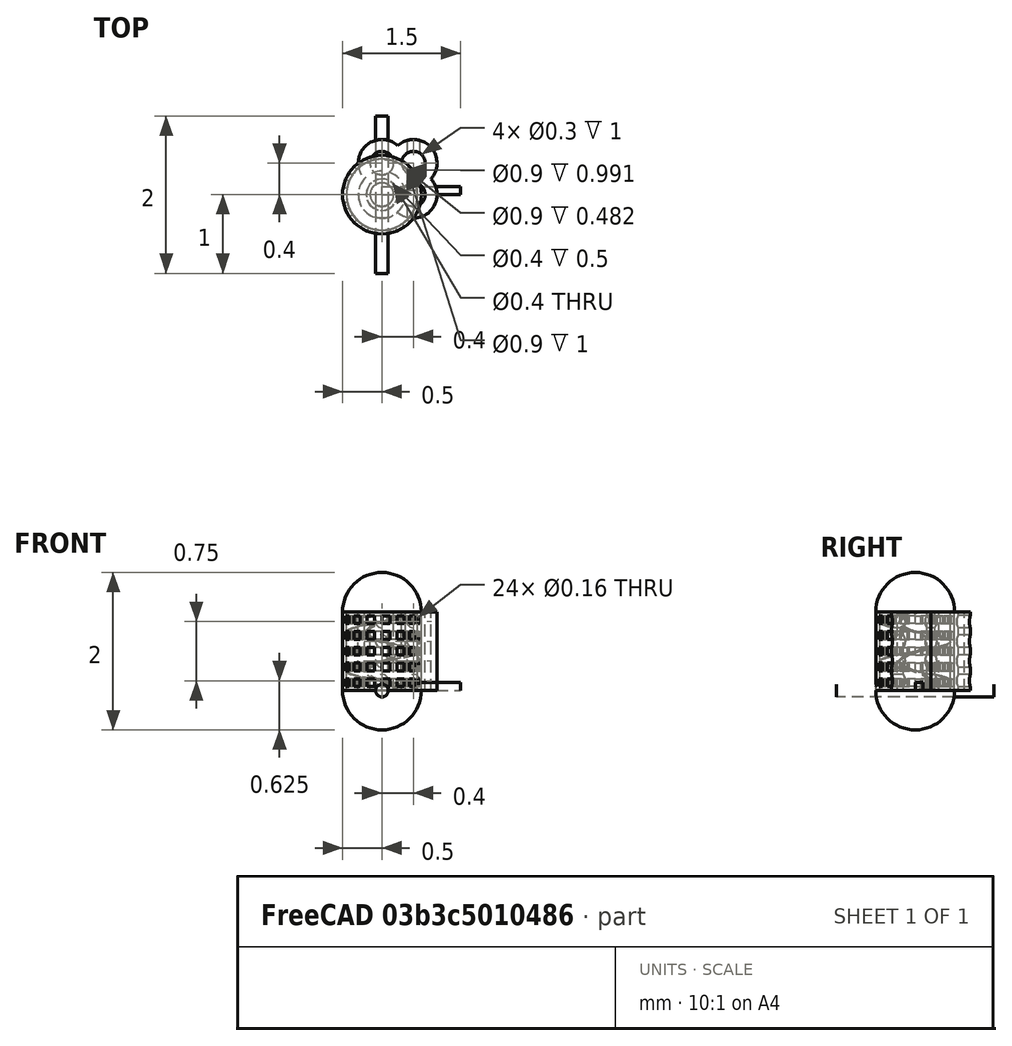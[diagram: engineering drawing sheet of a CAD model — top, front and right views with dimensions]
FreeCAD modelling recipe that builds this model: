
FCSTD DOCUMENT  (FreeCAD 0.19R24267 +99 (Git))
Label: models
License: All rights reserved
LicenseURL: http://en.wikipedia.org/wiki/All_rights_reserved
objects: Part::FeaturePython×12, Part::Cut×6, Part::Cylinder×6, Part::Box×2, Part::Sphere×2, Part::MultiFuse×2, Sketcher::SketchObject×2, PartDesign::AdditiveHelix×2, PartDesign::Body×2
note: 31 computed .brp shape members not serialized (recipe doc carries the construction recipe); baked Part::Feature solids carry a one-line shape summary decoded from their .brp

FEATURE [Part::FeaturePython] Tube  # WARN: FeaturePython — macro-defined, semantics opaque (R4)
  AttacherType = Attacher::AttachEngine3D
  Height = 1
  InnerRadius = 0.45
  OuterRadius = 0.5
FEATURE [Part::Box] Box  label="Cube"
  AttacherType = Attacher::AttachEngine3D
  Height = 0.1
  Length = 1
  Width = 0.1
FEATURE [Part::FeaturePython] Array  # Draft array (typed FeaturePython)
  Angle = 360
  ArrayType = 1
  Axis = (0,0,1)
  Base = -> Box
  Center = (0,0,0)
  Count = 16
  ExpandArray = false
  Fuse = false
  IntervalAxis = (0,0,0)
  IntervalX = (50,0,0)
  IntervalY = (0,50,0)
  IntervalZ = (0,0,50)
  NumberCircles = 3
  NumberPolar = 16
  NumberX = 2
  NumberY = 2
  NumberZ = 1
  PlacementList = 16 placements: [(0,0,0),(0,0,0),(0,0,0),(0,0,0),(0,0,0),(0,0,0),(0,0,0),(0,0,0),(0,0,0),(0,0,0),(0,0,0),(0,0,0),(0,0,0),(0,0,0),(0,0,0),(0,0,0)]
  RadialDistance = 50
  ScaleList = (16) [(1,1,1),(1,1,1),(1,1,1),(1,1,1),(1,1,1),(1,1,1),(1,1,1),(1,1,1),(1,1,1),(1,1,1),(1,1,1),(1,1,1),(1,1,1),(1,1,1),(1,1,1),(1,1,1)]
  Symmetry = 1
  TangentialDistance = 25
FEATURE [Part::FeaturePython] Array001  # Draft array (typed FeaturePython)
  Angle = 360
  ArrayType = 0
  Axis = (0,0,1)
  Base = -> Array
  Center = (0,0,0)
  Count = 5
  ExpandArray = false
  Fuse = false
  IntervalAxis = (0,0,0)
  IntervalX = (100,0,0)
  IntervalY = (0,100,0)
  IntervalZ = (0,0,0.2)
  NumberCircles = 3
  NumberPolar = 5
  NumberX = 1
  NumberY = 1
  NumberZ = 5
  Placement = pos=(0,0,0.05) rot=(0,0,1;0rad)
  PlacementList = 5 placements: arithmetic series from (0,0,0) step (0,0,0.2) to (0,0,0.8)
  RadialDistance = 50
  ScaleList = (5) [(1,1,1),(1,1,1),(1,1,1),(1,1,1),(1,1,1)]
  Symmetry = 1
  TangentialDistance = 25
FEATURE [Part::Cut] Cut
  Base = -> Tube
  Tool = -> Array001
FEATURE [Part::Cylinder] Cylinder
  Angle = 360
  AttacherType = Attacher::AttachEngine3D
  Height = 1
  Radius = 0.3
FEATURE [Part::FeaturePython] Array002  # Draft array (typed FeaturePython)
  Angle = 360
  ArrayType = 0
  Axis = (0,0,1)
  Base = -> Cylinder
  Center = (0,0,0)
  Count = 4
  ExpandArray = false
  Fuse = false
  IntervalAxis = (0,0,0)
  IntervalX = (0.4,0,0)
  IntervalY = (0,0.4,0)
  IntervalZ = (0,0,100)
  NumberCircles = 3
  NumberPolar = 5
  NumberX = 2
  NumberY = 2
  NumberZ = 1
  PlacementList = 4 placements: [(0,0,0),(0,0.4,0),(0.4,0,0),(0.4,0.4,0)]
  RadialDistance = 50
  ScaleList = (4) [(1,1,1),(1,1,1),(1,1,1),(1,1,1)]
  Symmetry = 1
  TangentialDistance = 25
FEATURE [Part::FeaturePython] Connect  # WARN: FeaturePython — macro-defined, semantics opaque (R4)
  Objects = -> [Array002]
  Tolerance = 0
FEATURE [Part::Cylinder] Cylinder001
  Angle = 360
  AttacherType = Attacher::AttachEngine3D
  Height = 1
  Radius = 0.15
FEATURE [Part::FeaturePython] Array003  # Draft array (typed FeaturePython)
  Angle = 360
  ArrayType = 0
  Axis = (0,0,1)
  Base = -> Cylinder001
  Center = (0,0,0)
  Count = 4
  ExpandArray = false
  Fuse = false
  IntervalAxis = (0,0,0)
  IntervalX = (0.4,0,0)
  IntervalY = (0,0.4,0)
  IntervalZ = (0,0,100)
  NumberCircles = 3
  NumberPolar = 5
  NumberX = 2
  NumberY = 2
  NumberZ = 1
  PlacementList = 4 placements: [(0,0,0),(0,0.4,0),(0.4,0,0),(0.4,0.4,0)]
  RadialDistance = 50
  ScaleList = (4) [(1,1,1),(1,1,1),(1,1,1),(1,1,1)]
  Symmetry = 1
  TangentialDistance = 25
FEATURE [Part::Cut] Cut001
  Base = -> Connect
  Tool = -> Array003
FEATURE [Part::Cylinder] Cylinder002
  Angle = 360
  AttacherType = Attacher::AttachEngine3D
  Height = 2
  Placement = pos=(0,1,0) rot=(1,0,0;1.5708rad)
  Radius = 0.08
FEATURE [Part::FeaturePython] Array004  # Draft array (typed FeaturePython)
  Angle = 360
  ArrayType = 0
  Axis = (0,0,1)
  Base = -> Cylinder002
  Center = (0,0,0)
  Count = 8
  ExpandArray = false
  Fuse = false
  IntervalAxis = (0,0,0)
  IntervalX = (0.4,0,0)
  IntervalY = (0,100,0)
  IntervalZ = (0,0,0.25)
  NumberCircles = 3
  NumberPolar = 5
  NumberX = 2
  NumberY = 1
  NumberZ = 4
  Placement = pos=(0,0,0.125) rot=(0,0,1;0rad)
  PlacementList = 8 placements: [(0,1,0),(0,1,0.25),(0,1,0.5),(0,1,0.75),(0.4,1,0),(0.4,1,0.25),(0.4,1,0.5),(0.4,1,0.75)]
  RadialDistance = 50
  ScaleList = (8) [(1,1,1),(1,1,1),(1,1,1),(1,1,1),(1,1,1),(1,1,1),(1,1,1),(1,1,1)]
  Symmetry = 1
  TangentialDistance = 25
FEATURE [Part::Cut] Cut002
  Base = -> Cut001
  Tool = -> Array004
FEATURE [Part::Sphere] Sphere
  Angle1 = -90
  Angle2 = 90
  Angle3 = 360
  AttacherType = Attacher::AttachEngine3D
  Radius = 0.5
FEATURE [Part::Cylinder] Cylinder003
  Angle = 360
  AttacherType = Attacher::AttachEngine3D
  Height = 1
  Radius = 0.5
FEATURE [Part::Sphere] Sphere001
  Angle1 = -90
  Angle2 = 90
  Angle3 = 360
  AttacherType = Attacher::AttachEngine3D
  Placement = pos=(0,0,1) rot=(0,0,1;0rad)
  Radius = 0.5
FEATURE [Part::MultiFuse] Fusion
  Shapes = -> [Sphere,Cylinder003]
FEATURE [Part::MultiFuse] Fusion001  label="capsule"
  Shapes = -> [Sphere001,Fusion]
FEATURE [Sketcher::SketchObject] Sketch
  FullyConstrained = true
  MapMode = 5
  Support = -> [XY_Plane]
  sketch-geometry (4):
    g0: LineSegment StartX=0 StartY=0 StartZ=0 EndX=0.45 EndY=0 EndZ=0
    g1: LineSegment StartX=0.45 StartY=0 StartZ=0 EndX=0.45 EndY=0.05 EndZ=0
    g2: LineSegment StartX=0.45 StartY=0.05 StartZ=0 EndX=0 EndY=0.05 EndZ=0
    g3: LineSegment StartX=0 StartY=0.05 StartZ=0 EndX=0 EndY=0 EndZ=0
  constraints (11):
    c: Coincident(g0,g1)
    c: Coincident(g1,g2)
    c: Coincident(g2,g3)
    c: Coincident(g3,g0)
    c: Horizontal(g0)
    c: Horizontal(g2)
    c: Vertical(g1)
    c: Vertical(g3)
    c: Coincident(g0,g-1)
    c: Distance(g2) = 0.45
    c: DistanceY(g-1,g1) = 0.05
FEATURE [PartDesign::AdditiveHelix] AdditiveHelix
  Angle = 0
  Axis = (-3e-16,3e-16,1)
  Base = (0,0,0)
  HasBeenEdited = true
  Height = 1
  LeftHanded = false
  Mode = 0
  Outside = false
  Pitch = 0.5
  Profile = -> Sketch
  ReferenceAxis = -> Z_Axis
  Turns = 2
FEATURE [PartDesign::Body] Body
  Group = -> [Sketch,AdditiveHelix]
  Origin = -> Origin
  Tip = -> AdditiveHelix
FEATURE [Part::Cylinder] Cylinder004
  Angle = 360
  AttacherType = Attacher::AttachEngine3D
  Height = 2
  Radius = 0.2
FEATURE [Part::Cut] Cut003
  Base = -> Body
  Tool = -> Cylinder004
FEATURE [Part::Box] Box001  label="Cube001"
  AttacherType = Attacher::AttachEngine3D
  Height = 0.1
  Length = 1
  Width = 0.1
FEATURE [Part::FeaturePython] Tube001  # WARN: FeaturePython — macro-defined, semantics opaque (R4)
  AttacherType = Attacher::AttachEngine3D
  Height = 1
  InnerRadius = 0.45
  OuterRadius = 0.5
FEATURE [Part::FeaturePython] Array005  # Draft array (typed FeaturePython)
  Angle = 360
  ArrayType = 1
  Axis = (0,0,1)
  Base = -> Box001
  Center = (0,0,0)
  Count = 16
  ExpandArray = false
  Fuse = false
  IntervalAxis = (0,0,0)
  IntervalX = (50,0,0)
  IntervalY = (0,50,0)
  IntervalZ = (0,0,50)
  NumberCircles = 3
  NumberPolar = 16
  NumberX = 2
  NumberY = 2
  NumberZ = 1
  PlacementList = 16 placements: [(0,0,0),(0,0,0),(0,0,0),(0,0,0),(0,0,0),(0,0,0),(0,0,0),(0,0,0),(0,0,0),(0,0,0),(0,0,0),(0,0,0),(0,0,0),(0,0,0),(0,0,0),(0,0,0)]
  RadialDistance = 50
  ScaleList = (16) [(1,1,1),(1,1,1),(1,1,1),(1,1,1),(1,1,1),(1,1,1),(1,1,1),(1,1,1),(1,1,1),(1,1,1),(1,1,1),(1,1,1),(1,1,1),(1,1,1),(1,1,1),(1,1,1)]
  Symmetry = 1
  TangentialDistance = 25
FEATURE [Part::FeaturePython] Array006  # Draft array (typed FeaturePython)
  Angle = 360
  ArrayType = 0
  Axis = (0,0,1)
  Base = -> Array005
  Center = (0,0,0)
  Count = 5
  ExpandArray = false
  Fuse = false
  IntervalAxis = (0,0,0)
  IntervalX = (100,0,0)
  IntervalY = (0,100,0)
  IntervalZ = (0,0,0.2)
  NumberCircles = 3
  NumberPolar = 5
  NumberX = 1
  NumberY = 1
  NumberZ = 5
  Placement = pos=(0,0,0.05) rot=(0,0,1;0rad)
  PlacementList = 5 placements: arithmetic series from (0,0,0) step (0,0,0.2) to (0,0,0.8)
  RadialDistance = 50
  ScaleList = (5) [(1,1,1),(1,1,1),(1,1,1),(1,1,1),(1,1,1)]
  Symmetry = 1
  TangentialDistance = 25
FEATURE [Part::FeaturePython] XOR  # WARN: FeaturePython — macro-defined, semantics opaque (R4)
  Objects = -> [Array006,Cut003]
  Tolerance = 0
FEATURE [Part::Cut] Cut004
  Base = -> Tube001
  Tool = -> XOR
FEATURE [Sketcher::SketchObject] Sketch001
  FullyConstrained = true
  MapMode = 5
  Support = -> [XY_Plane001]
  sketch-geometry (4):
    g0: LineSegment StartX=0 StartY=0 StartZ=0 EndX=0.45 EndY=0 EndZ=0
    g1: LineSegment StartX=0.45 StartY=0 StartZ=0 EndX=0.45 EndY=0.05 EndZ=0
    g2: LineSegment StartX=0.45 StartY=0.05 StartZ=0 EndX=0 EndY=0.05 EndZ=0
    g3: LineSegment StartX=0 StartY=0.05 StartZ=0 EndX=0 EndY=0 EndZ=0
  constraints (11):
    c: Coincident(g0,g1)
    c: Coincident(g1,g2)
    c: Coincident(g2,g3)
    c: Coincident(g3,g0)
    c: Horizontal(g0)
    c: Horizontal(g2)
    c: Vertical(g1)
    c: Vertical(g3)
    c: Coincident(g0,g-1)
    c: Distance(g2) = 0.45
    c: DistanceY(g-1,g1) = 0.05
FEATURE [PartDesign::AdditiveHelix] AdditiveHelix001
  Angle = 0
  Axis = (-3e-16,3e-16,1)
  Base = (0,0,0)
  HasBeenEdited = true
  Height = 1
  LeftHanded = false
  Mode = 0
  Outside = false
  Pitch = 0.5
  Profile = -> Sketch001
  ReferenceAxis = -> Z_Axis001
  Turns = 2
FEATURE [PartDesign::Body] Body001
  Group = -> [Sketch001,AdditiveHelix001]
  Origin = -> Origin001
  Tip = -> AdditiveHelix001
FEATURE [Part::Cylinder] Cylinder005
  Angle = 360
  AttacherType = Attacher::AttachEngine3D
  Height = 2
  Radius = 0.2
FEATURE [Part::Cut] Cut005
  Base = -> Body001
  Tool = -> Cylinder005
FEATURE [Part::FeaturePython] BooleanFragments  # WARN: FeaturePython — macro-defined, semantics opaque (R4)
  Mode = 0
  Objects = -> [Cut004,Cut005]
  Tolerance = 0
